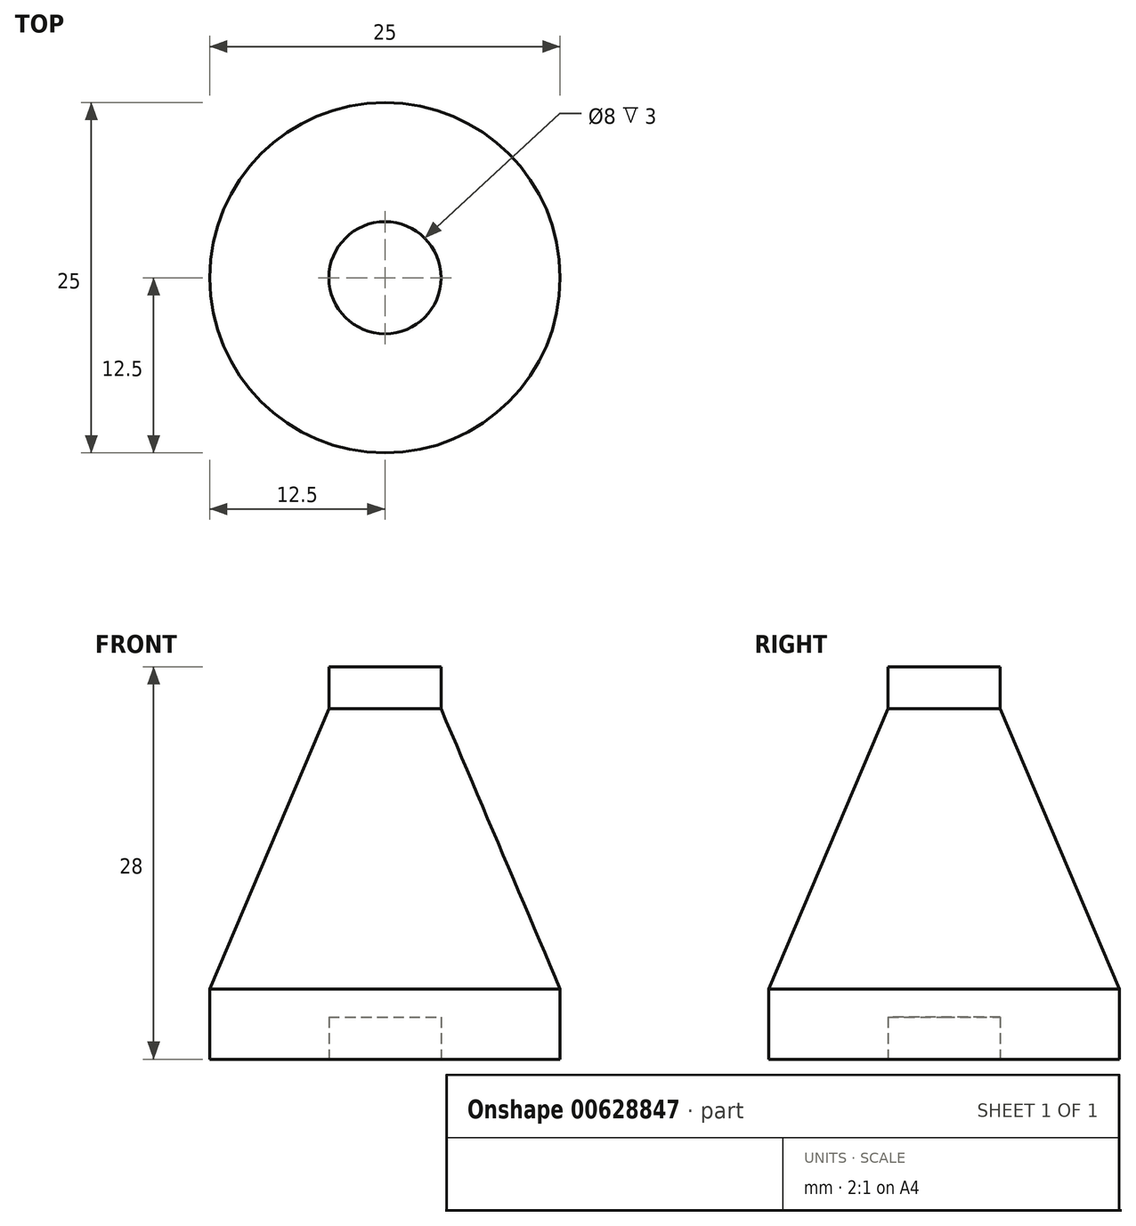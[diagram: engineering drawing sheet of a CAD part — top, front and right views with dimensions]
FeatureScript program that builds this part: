
annotation { "Feature Type Name" : "Feature", "Feature Type Description" : "" }
export const myFeature = defineFeature(function(context is Context, id is Id, definition is map)
    precondition{}
    {
        {
            var Q0;
            Q0=qCreatedBy(makeId("Front.planeOp"),FACE);
            var sketch = newSketch(context, id + "F0", { "sketchPlane" : qUnion([Q0])});
            skLineSegment(sketch, "E0", {"start": v(0, 0) * mm, "end": v(12.5, 0) * mm});
            skLineSegment(sketch, "E1", {"start": v(12.5, 0) * mm, "end": v(12.5, 5) * mm});
            skLineSegment(sketch, "E2", {"start": v(12.5, 5) * mm, "end": v(4, 25) * mm});
            skLineSegment(sketch, "E3", {"start": v(4, 25) * mm, "end": v(0, 25) * mm});
            skLineSegment(sketch, "E4", {"start": v(0, 25) * mm, "end": v(0, 0) * mm});
            skSolve(sketch);
        }
        {
            var Q0;
            Q0=makeQuery(id+"F0.imprint","IMPRINT",FACE,{"disambiguationData":[TD([[makeQuery(id+"F0.imprint","IMPRINT",EDGE,{"derivedFrom":sQuery(id+"F0.wireOp",EDGE,"E0")}),1.0]])]});
            var Q1;
            Q1=sQuery(id+"F0.wireOp",EDGE,"E4");
            revolve(context, id + "F1", {"entities" : qUnion([Q0]), "axis" : qUnion([Q1]), "revolveType" : RevolveType.FULL});
        }
        {
            var Q0;
            Q0=makeQuery(id+"F1.opRevolve","SWEPT_FACE",FACE,{"disambiguationData":[OSD([sQuery(id+"F0.wireOp",EDGE,"E3")])]});
            var sketch = newSketch(context, id + "F2", { "sketchPlane" : qUnion([Q0])});
            skCircle(sketch, "E5", {"center": v(0, 0) * mm, "radius": 4 * mm});
            skSolve(sketch);
        }
        {
            var Q0;
            Q0 = qSketchRegion(id + "F2", true);
            extrude(context, id + "F3", {"entities" : qUnion([Q0]), "operationType" : NewBodyOperationType.ADD, "depth" : 3 * mm, "offsetDistance" : 25 * mm});
        }
        {
            var Q0;
            Q0=makeQuery(id+"F1.opRevolve","SWEPT_FACE",FACE,{"disambiguationData":[OSD([sQuery(id+"F0.wireOp",EDGE,"E0")])]});
            var sketch = newSketch(context, id + "F4", { "sketchPlane" : qUnion([Q0])});
            skCircle(sketch, "E6", {"center": v(0, 0) * mm, "radius": 4 * mm});
            skSolve(sketch);
        }
        {
            var Q0;
            Q0 = qSketchRegion(id + "F4", true);
            extrude(context, id + "F5", {"entities" : qUnion([Q0]), "operationType" : NewBodyOperationType.REMOVE, "oppositeDirection" : true, "depth" : 3 * mm, "offsetDistance" : 25 * mm});
        }
    });
